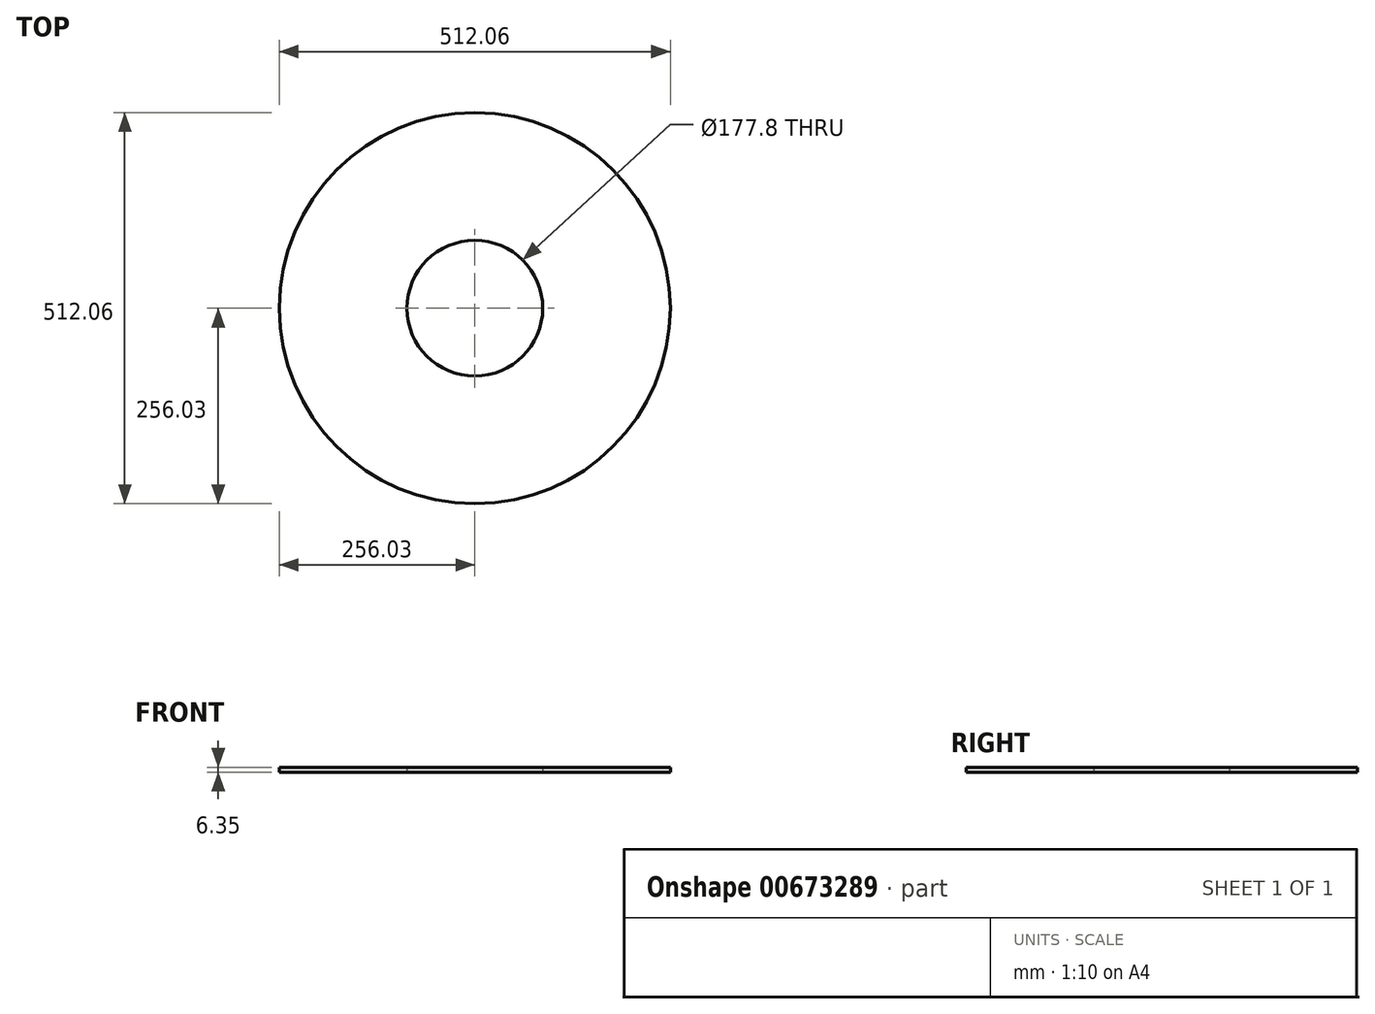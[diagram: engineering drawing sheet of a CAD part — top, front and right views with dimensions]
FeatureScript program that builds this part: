
annotation { "Feature Type Name" : "Feature", "Feature Type Description" : "" }
export const myFeature = defineFeature(function(context is Context, id is Id, definition is map)
    precondition{}
    {
        {
            var Q0;
            Q0=qCreatedBy(makeId("Top.planeOp"),FACE);
            var sketch = newSketch(context, id + "F0", { "sketchPlane" : qUnion([Q0])});
            skCircle(sketch, "E0", {"center": v(0, 0) * mm, "radius": 256.03 * mm});
            skCircle(sketch, "E1", {"center": v(0, 0) * mm, "radius": 117.48 * mm});
            skCircle(sketch, "E2", {"center": v(0, 0) * mm, "radius": 88.9 * mm});
            skSolve(sketch);
        }
        {
            var Q0;
            Q0=makeQuery(id+"F0.imprint","IMPRINT",FACE,{"disambiguationData":[TD([[makeQuery(id+"F0.imprint","IMPRINT",EDGE,{"derivedFrom":sQuery(id+"F0.wireOp",EDGE,"E0")}),1.0]])]});
            var Q1;
            Q1=makeQuery(id+"F0.imprint","IMPRINT",FACE,{"disambiguationData":[TD([[makeQuery(id+"F0.imprint","IMPRINT",EDGE,{"derivedFrom":sQuery(id+"F0.wireOp",EDGE,"E1")}),1.0]])]});
            extrude(context, id + "F1", {"entities" : qUnion([Q0, Q1]), "depth" : 6.35 * mm, "offsetDistance" : 25.4 * mm});
        }
    });
